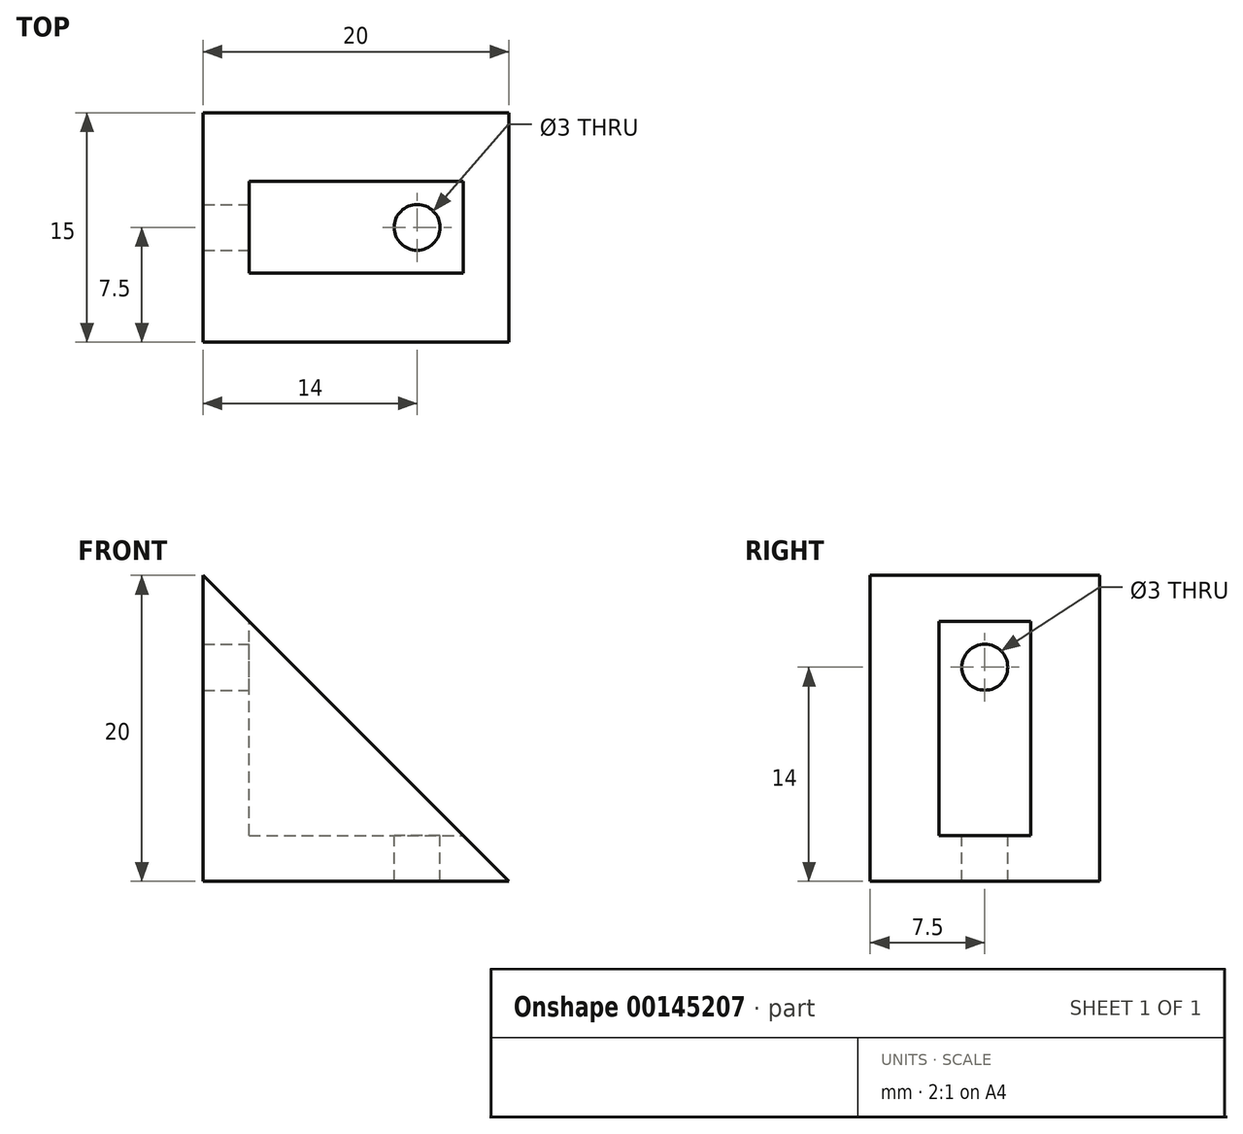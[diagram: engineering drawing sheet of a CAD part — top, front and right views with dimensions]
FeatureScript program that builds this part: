
annotation { "Feature Type Name" : "Feature", "Feature Type Description" : "" }
export const myFeature = defineFeature(function(context is Context, id is Id, definition is map)
    precondition{}
    {
        {
            var Q0;
            Q0=qCreatedBy(makeId("Front.planeOp"),FACE);
            var sketch = newSketch(context, id + "F0", { "sketchPlane" : qUnion([Q0])});
            skLineSegment(sketch, "E0", {"start": v(0, 0) * mm, "end": v(0, 20) * mm});
            skLineSegment(sketch, "E1", {"start": v(0, 0) * mm, "end": v(20, 0) * mm});
            skLineSegment(sketch, "E2", {"start": v(20, 0) * mm, "end": v(0, 20) * mm});
            skSolve(sketch);
        }
        {
            var Q0;
            Q0 = qSketchRegion(id + "F0", true);
            extrude(context, id + "F1", {"entities" : qUnion([Q0]), "depth" : 4.5 * mm});
        }
        {
            var Q0;
            Q0=makeQuery(id+"F1.opExtrude","CAP_FACE",FACE,{"disambiguationData":[OSD([sQuery(id+"F0.wireOp",EDGE,"E0"),sQuery(id+"F0.wireOp",EDGE,"E1"),sQuery(id+"F0.wireOp",EDGE,"E2")])],"isStart":false});
            var sketch = newSketch(context, id + "F2", { "sketchPlane" : qUnion([Q0])});
            skLineSegment(sketch, "E3.0", {"start": v(3, 3) * mm, "end": v(3, 15) * mm});
            skLineSegment(sketch, "E3.1", {"start": v(3, 3) * mm, "end": v(15, 3) * mm});
            skLineSegment(sketch, "E4", {"start": v(20, 0) * mm, "end": v(17, 3) * mm});
            skLineSegment(sketch, "E5", {"start": v(3, 17) * mm, "end": v(0, 20) * mm});
            skLineSegment(sketch, "E6", {"start": v(0, 20) * mm, "end": v(0, 0) * mm});
            skLineSegment(sketch, "E7", {"start": v(0, 0) * mm, "end": v(20, 0) * mm});
            skLineSegment(sketch, "E8", {"start": v(3, 15) * mm, "end": v(3, 17) * mm});
            skLineSegment(sketch, "E9", {"start": v(15, 3) * mm, "end": v(17, 3) * mm});
            skSolve(sketch);
        }
        {
            var Q0;
            Q0 = qSketchRegion(id + "F2", true);
            extrude(context, id + "F3", {"entities" : qUnion([Q0]), "operationType" : NewBodyOperationType.ADD, "depth" : 6 * mm});
        }
        {
            var Q0;
            Q0=makeQuery(id+"F3.opExtrude","CAP_FACE",FACE,{"disambiguationData":[OSD([sQuery(id+"F2.wireOp",EDGE,"E3.0"),sQuery(id+"F2.wireOp",EDGE,"E3.1"),sQuery(id+"F2.wireOp",EDGE,"E4"),sQuery(id+"F2.wireOp",EDGE,"E5"),sQuery(id+"F2.wireOp",EDGE,"E6"),sQuery(id+"F2.wireOp",EDGE,"E7"),sQuery(id+"F2.wireOp",EDGE,"E8"),sQuery(id+"F2.wireOp",EDGE,"E9")])],"isStart":false});
            var sketch = newSketch(context, id + "F4", { "sketchPlane" : qUnion([Q0])});
            skLineSegment(sketch, "E10", {"start": v(0, 20) * mm, "end": v(20, 0) * mm});
            skLineSegment(sketch, "E11", {"start": v(20, 0) * mm, "end": v(0, 0) * mm});
            skLineSegment(sketch, "E12", {"start": v(0, 0) * mm, "end": v(0, 20) * mm});
            skSolve(sketch);
        }
        {
            var Q0;
            Q0 = qSketchRegion(id + "F4", true);
            extrude(context, id + "F5", {"entities" : qUnion([Q0]), "operationType" : NewBodyOperationType.ADD, "depth" : 4.5 * mm});
        }
        {
            var Q0;
            Q0=makeQuery(id+"F3.opExtrude","SWEPT_FACE",FACE,{"disambiguationData":[OSD([sQuery(id+"F2.wireOp",EDGE,"E3.0"),sQuery(id+"F2.wireOp",EDGE,"E8")])]});
            var sketch = newSketch(context, id + "F6", { "sketchPlane" : qUnion([Q0])});
            skLineSegment(sketch, "E13", {"start": v(-7.5, 17) * mm, "end": v(-7.5, 14) * mm});
            skCircle(sketch, "E14", {"center": v(-7.5, 14) * mm, "radius": 1.5 * mm});
            skSolve(sketch);
        }
        {
            var Q0;
            Q0 = qSketchRegion(id + "F6", true);
            extrude(context, id + "F7", {"entities" : qUnion([Q0]), "operationType" : NewBodyOperationType.REMOVE, "endBound" : BoundingType.THROUGH_ALL, "oppositeDirection" : true, "depth" : 25 * mm});
        }
        {
            var Q0;
            Q0=makeQuery(id+"F3.opExtrude","SWEPT_FACE",FACE,{"disambiguationData":[OSD([sQuery(id+"F2.wireOp",EDGE,"E3.1"),sQuery(id+"F2.wireOp",EDGE,"E9")])]});
            var sketch = newSketch(context, id + "F8", { "sketchPlane" : qUnion([Q0])});
            skLineSegment(sketch, "E15", {"start": v(17, -7.5) * mm, "end": v(14, -7.5) * mm});
            skCircle(sketch, "E16", {"center": v(14, -7.5) * mm, "radius": 1.5 * mm});
            skSolve(sketch);
        }
        {
            var Q0;
            Q0 = qSketchRegion(id + "F8", true);
            extrude(context, id + "F9", {"entities" : qUnion([Q0]), "operationType" : NewBodyOperationType.REMOVE, "oppositeDirection" : true, "depth" : 25 * mm});
        }
    });
